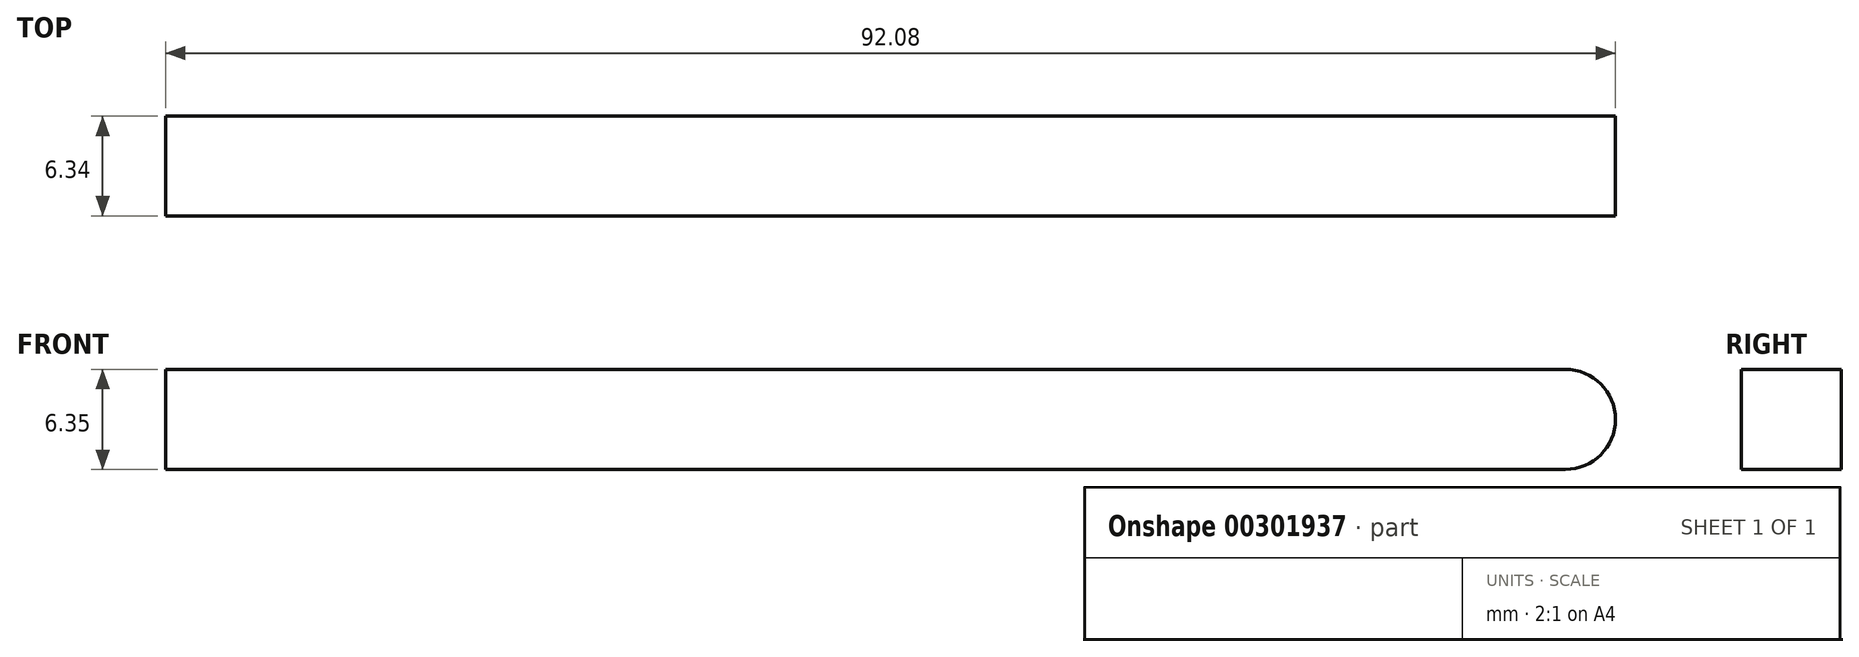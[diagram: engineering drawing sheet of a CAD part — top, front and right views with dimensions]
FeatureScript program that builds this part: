
annotation { "Feature Type Name" : "Feature", "Feature Type Description" : "" }
export const myFeature = defineFeature(function(context is Context, id is Id, definition is map)
    precondition{}
    {
        {
            var Q0;
            Q0=qCreatedBy(makeId("Front.planeOp"),FACE);
            var sketch = newSketch(context, id + "F0", { "sketchPlane" : qUnion([Q0])});
            skLineSegment(sketch, "E0", {"start": v(-42.44, 23.1) * mm, "end": v(46.46, 23.1) * mm});
            skLineSegment(sketch, "E1", {"start": v(-42.44, 23.1) * mm, "end": v(-42.44, 16.74) * mm});
            skLineSegment(sketch, "E2", {"start": v(-42.44, 16.74) * mm, "end": v(46.46, 16.74) * mm});
            skArc(sketch, "E3", {"start": v(46.46, 16.74) * mm, "mid": v(49.64, 19.92) * mm, "end": v(46.46, 23.1) * mm});
            skSolve(sketch);
        }
        {
            var Q0;
            Q0 = qSketchRegion(id + "F0", true);
            extrude(context, id + "F1", {"entities" : qUnion([Q0]), "endBound" : BoundingType.SYMMETRIC, "depth" : 6.35 * mm});
        }
    });
